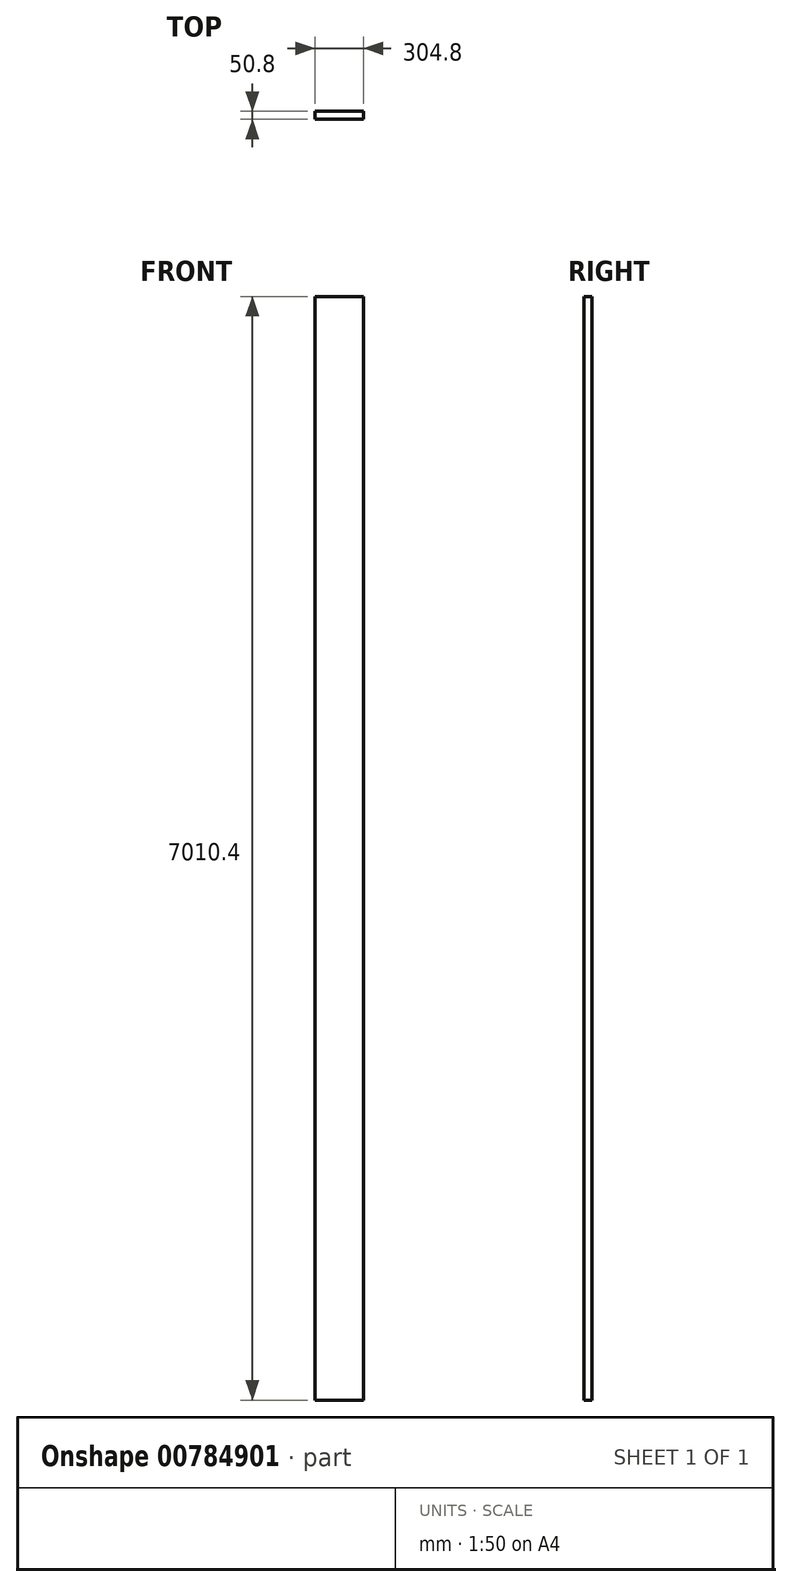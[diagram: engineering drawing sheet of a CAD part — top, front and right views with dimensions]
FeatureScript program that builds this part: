
annotation { "Feature Type Name" : "Feature", "Feature Type Description" : "" }
export const myFeature = defineFeature(function(context is Context, id is Id, definition is map)
    precondition{}
    {
        {
            var Q0;
            Q0=qCreatedBy(makeId("Front.planeOp"),FACE);
            var sketch = newSketch(context, id + "F0", { "sketchPlane" : qUnion([Q0])});
            skLineSegment(sketch, "E0.bottom", {"start": v(152.4, 3505.2) * mm, "end": v(-152.4, 3505.2) * mm});
            skLineSegment(sketch, "E0.top", {"start": v(152.4, -3505.2) * mm, "end": v(-152.4, -3505.2) * mm});
            skLineSegment(sketch, "E0.left", {"start": v(152.4, 3505.2) * mm, "end": v(152.4, -3505.2) * mm});
            skLineSegment(sketch, "E0.right", {"start": v(-152.4, 3505.2) * mm, "end": v(-152.4, -3505.2) * mm});
            skPoint(sketch, "E0.middle", {"position": v(0, 0) * mm});
            skSolve(sketch);
        }
        {
            var Q0;
            Q0=makeQuery(id+"F0.imprint","IMPRINT",FACE,{"disambiguationData":[TD([[makeQuery(id+"F0.imprint","IMPRINT",EDGE,{"derivedFrom":sQuery(id+"F0.wireOp",EDGE,"E0.bottom")}),1.0]])]});
            extrude(context, id + "F1", {"entities" : qUnion([Q0]), "depth" : 50.8 * mm, "offsetDistance" : 25.4 * mm});
        }
    });
